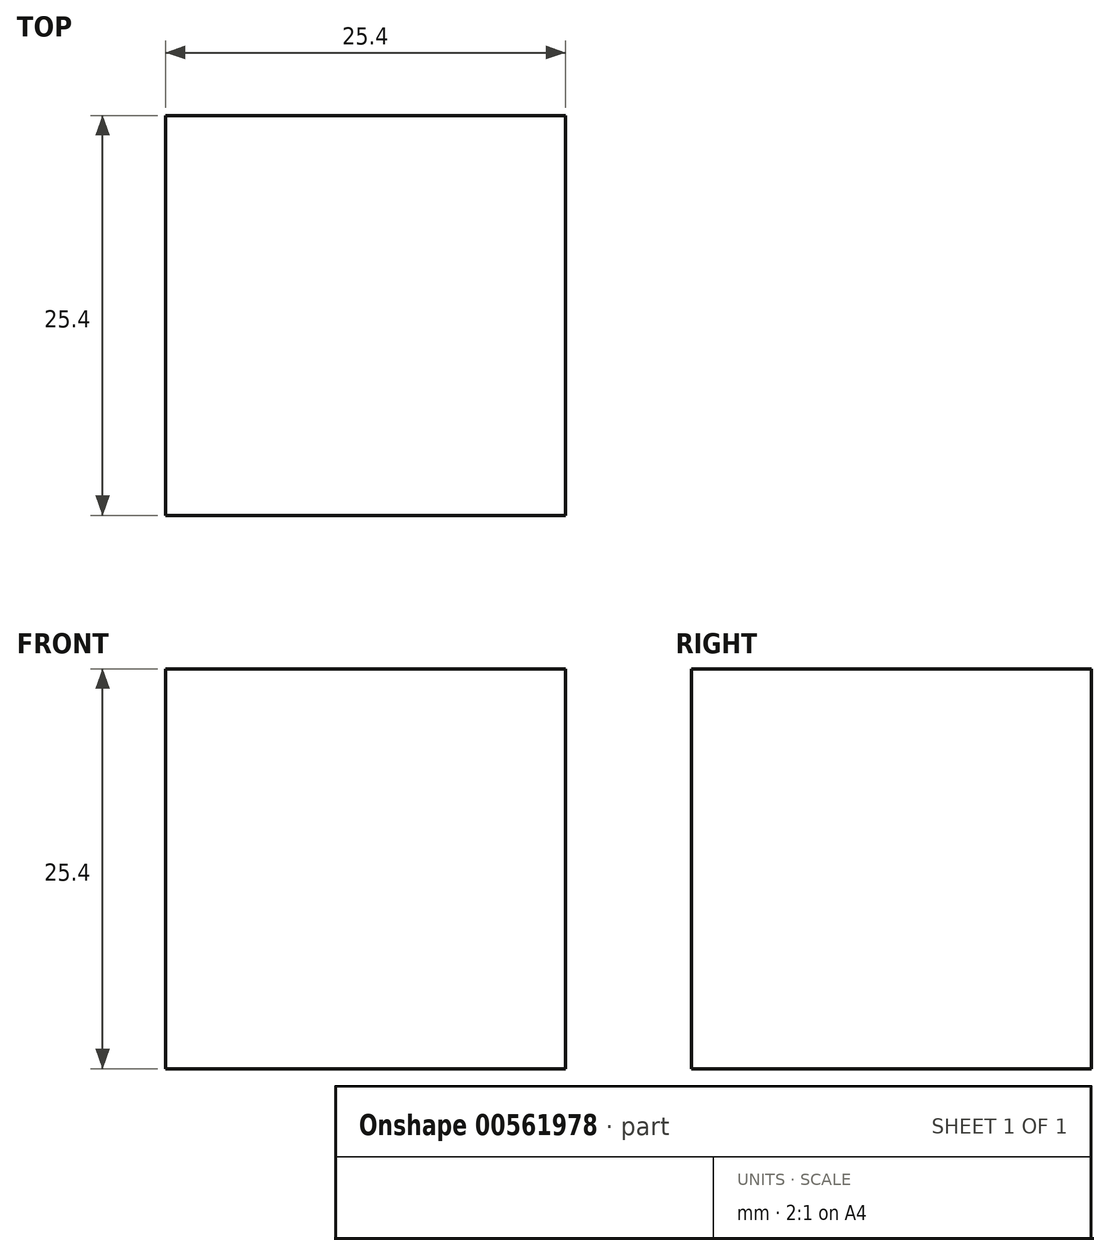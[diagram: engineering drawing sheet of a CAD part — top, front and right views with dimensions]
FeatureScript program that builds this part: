
annotation { "Feature Type Name" : "Feature", "Feature Type Description" : "" }
export const myFeature = defineFeature(function(context is Context, id is Id, definition is map)
    precondition{}
    {
        {
            var Q0;
            Q0=qCreatedBy(makeId("Front.planeOp"),FACE);
            var sketch = newSketch(context, id + "F0", { "sketchPlane" : qUnion([Q0])});
            skLineSegment(sketch, "E0.bottom", {"start": v(-25.4, 39.18) * mm, "end": v(0, 39.18) * mm});
            skLineSegment(sketch, "E0.top", {"start": v(-25.4, 13.78) * mm, "end": v(0, 13.78) * mm});
            skLineSegment(sketch, "E0.left", {"start": v(-25.4, 39.18) * mm, "end": v(-25.4, 13.78) * mm});
            skLineSegment(sketch, "E0.right", {"start": v(0, 39.18) * mm, "end": v(0, 13.78) * mm});
            skSolve(sketch);
        }
        {
            var Q0;
            Q0=makeQuery(id+"F0.imprint","IMPRINT",FACE,{"disambiguationData":[TD([[makeQuery(id+"F0.imprint","IMPRINT",EDGE,{"derivedFrom":sQuery(id+"F0.wireOp",EDGE,"E0.bottom")}),-1.0]])]});
            extrude(context, id + "F1", {"entities" : qUnion([Q0]), "depth" : 25.4 * mm, "offsetDistance" : 25.4 * mm});
        }
    });
